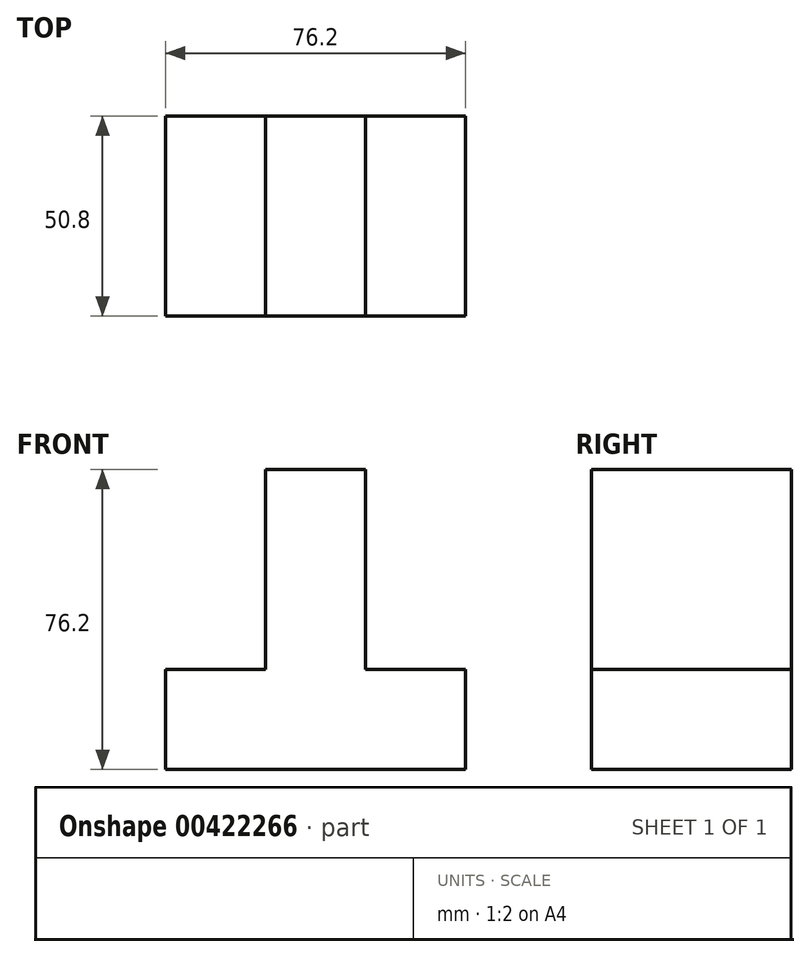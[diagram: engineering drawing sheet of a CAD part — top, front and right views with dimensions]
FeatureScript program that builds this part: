
annotation { "Feature Type Name" : "Feature", "Feature Type Description" : "" }
export const myFeature = defineFeature(function(context is Context, id is Id, definition is map)
    precondition{}
    {
        {
            var Q0;
            Q0=qCreatedBy(makeId("Front.planeOp"),FACE);
            var sketch = newSketch(context, id + "F0", { "sketchPlane" : qUnion([Q0])});
            skLineSegment(sketch, "E0", {"start": v(0, 0) * mm, "end": v(-76.2, 0) * mm});
            skLineSegment(sketch, "E1", {"start": v(-76.2, 0) * mm, "end": v(-76.2, 25.4) * mm});
            skLineSegment(sketch, "E2", {"start": v(-76.2, 25.4) * mm, "end": v(-50.8, 25.4) * mm});
            skLineSegment(sketch, "E3", {"start": v(-50.8, 25.4) * mm, "end": v(-50.8, 76.2) * mm});
            skLineSegment(sketch, "E4", {"start": v(-50.8, 76.2) * mm, "end": v(-25.4, 76.2) * mm});
            skLineSegment(sketch, "E5", {"start": v(-25.4, 76.2) * mm, "end": v(-25.4, 25.4) * mm});
            skLineSegment(sketch, "E6", {"start": v(-25.4, 25.4) * mm, "end": v(0, 25.4) * mm});
            skLineSegment(sketch, "E7", {"start": v(0, 25.4) * mm, "end": v(0, 0) * mm});
            skSolve(sketch);
        }
        {
            var Q0;
            Q0=makeQuery(id+"F0.imprint","IMPRINT",FACE,{"disambiguationData":[TD([[makeQuery(id+"F0.imprint","IMPRINT",EDGE,{"derivedFrom":sQuery(id+"F0.wireOp",EDGE,"E0")}),-1.0]])]});
            var Q1;
            Q1=makeQuery(id+"F0.imprint","IMPRINT",FACE,{"disambiguationData":[TD([[makeQuery(id+"F0.imprint","IMPRINT",EDGE,{"derivedFrom":sQuery(id+"F0.wireOp",EDGE,"E0")}),-1.0]])]});
            extrude(context, id + "F1", {"entities" : qUnion([Q0, Q1]), "depth" : 50.8 * mm});
        }
    });
